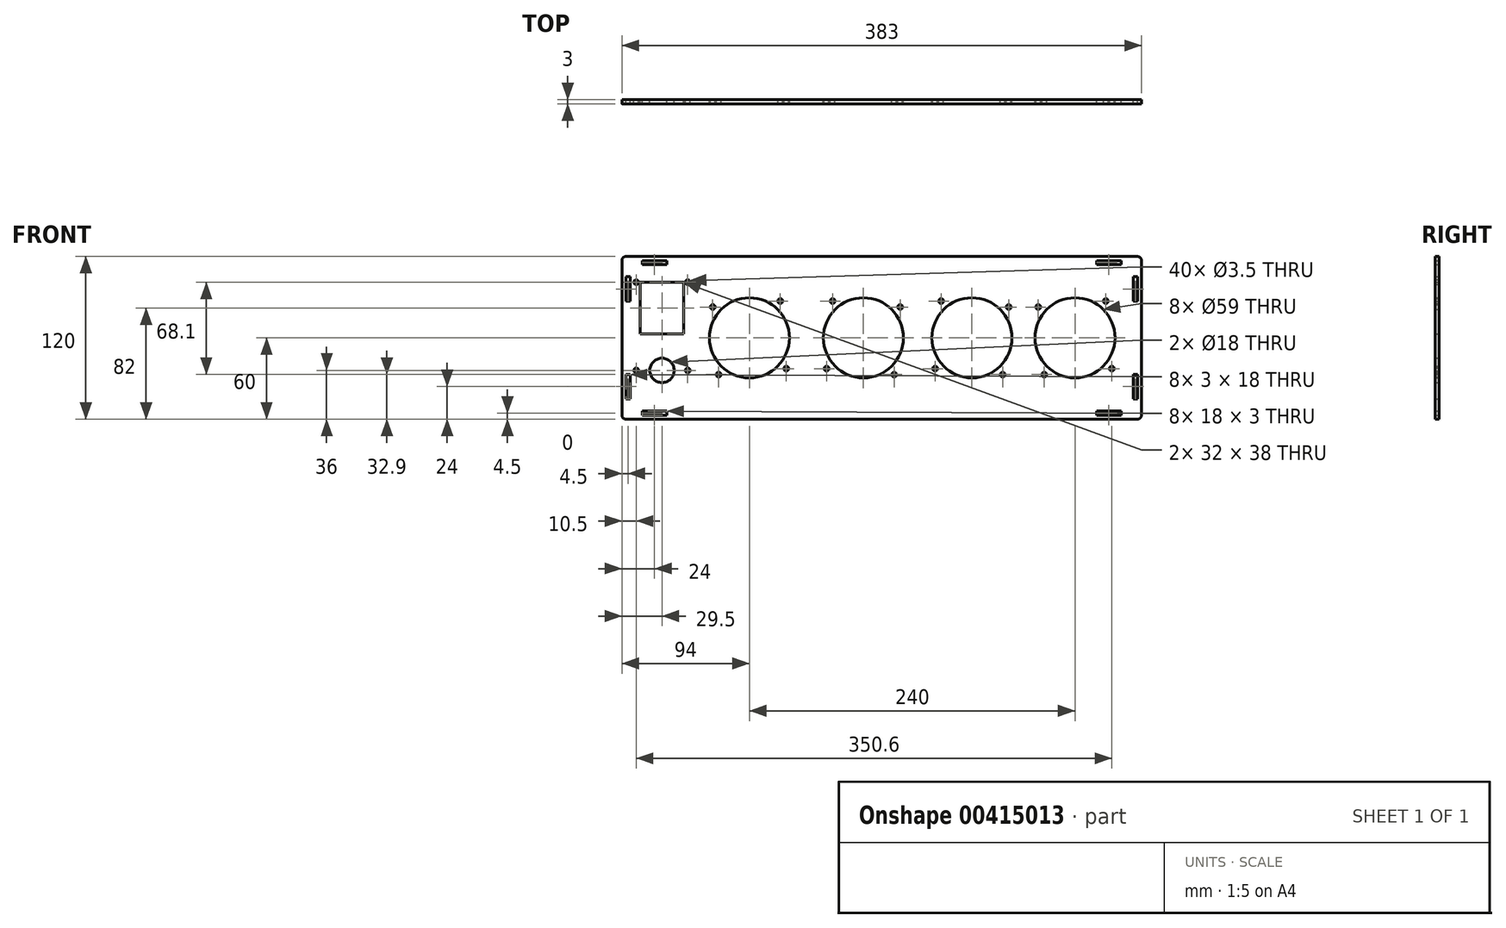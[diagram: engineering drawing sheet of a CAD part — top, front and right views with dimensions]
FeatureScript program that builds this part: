
annotation { "Feature Type Name" : "Feature", "Feature Type Description" : "" }
export const myFeature = defineFeature(function(context is Context, id is Id, definition is map)
    precondition{}
    {
        {
            var Q0;
            Q0=qCreatedBy(makeId("Front.planeOp"),FACE);
            var sketch = newSketch(context, id + "F0", { "sketchPlane" : qUnion([Q0])});
            skLineSegment(sketch, "E0.bottom", {"start": v(-188.5, 60) * mm, "end": v(188.5, 60) * mm});
            skLineSegment(sketch, "E0.top", {"start": v(-188.5, -60) * mm, "end": v(188.5, -60) * mm});
            skLineSegment(sketch, "E0.left", {"start": v(-191.5, 57) * mm, "end": v(-191.5, -57) * mm});
            skLineSegment(sketch, "E0.right", {"start": v(191.5, 57) * mm, "end": v(191.5, -57) * mm});
            skPoint(sketch, "E1.visualSharp", {"position": v(-191.5, 60) * mm});
            skArc(sketch, "E1.filletArc", {"start": v(-188.5, 60) * mm, "mid": v(-190.62, 59.12) * mm, "end": v(-191.5, 57) * mm});
            skPoint(sketch, "E2.visualSharp", {"position": v(191.5, 60) * mm});
            skArc(sketch, "E2.filletArc", {"start": v(191.5, 57) * mm, "mid": v(190.62, 59.12) * mm, "end": v(188.5, 60) * mm});
            skPoint(sketch, "E3.visualSharp", {"position": v(191.5, -60) * mm});
            skArc(sketch, "E3.filletArc", {"start": v(188.5, -60) * mm, "mid": v(190.62, -59.12) * mm, "end": v(191.5, -57) * mm});
            skPoint(sketch, "E4.visualSharp", {"position": v(-191.5, -60) * mm});
            skArc(sketch, "E4.filletArc", {"start": v(-191.5, -57) * mm, "mid": v(-190.62, -59.12) * mm, "end": v(-188.5, -60) * mm});
            skLineSegment(sketch, "E5.bottom", {"start": v(-176.5, 57) * mm, "end": v(-158.5, 57) * mm});
            skLineSegment(sketch, "E5.top", {"start": v(-176.5, 54) * mm, "end": v(-158.5, 54) * mm});
            skLineSegment(sketch, "E5.left", {"start": v(-176.5, 57) * mm, "end": v(-176.5, 54) * mm});
            skLineSegment(sketch, "E5.right", {"start": v(-158.5, 57) * mm, "end": v(-158.5, 54) * mm});
            skLineSegment(sketch, "E6.bottom", {"start": v(158.5, 57) * mm, "end": v(176.5, 57) * mm});
            skLineSegment(sketch, "E6.top", {"start": v(158.5, 54) * mm, "end": v(176.5, 54) * mm});
            skLineSegment(sketch, "E6.left", {"start": v(158.5, 57) * mm, "end": v(158.5, 54) * mm});
            skLineSegment(sketch, "E6.right", {"start": v(176.5, 57) * mm, "end": v(176.5, 54) * mm});
            skLineSegment(sketch, "E7.bottom", {"start": v(188.5, 45) * mm, "end": v(185.5, 45) * mm});
            skLineSegment(sketch, "E7.top", {"start": v(188.5, 27) * mm, "end": v(185.5, 27) * mm});
            skLineSegment(sketch, "E7.left", {"start": v(188.5, 45) * mm, "end": v(188.5, 27) * mm});
            skLineSegment(sketch, "E7.right", {"start": v(185.5, 45) * mm, "end": v(185.5, 27) * mm});
            skLineSegment(sketch, "E8.bottom", {"start": v(188.5, -27) * mm, "end": v(185.5, -27) * mm});
            skLineSegment(sketch, "E8.top", {"start": v(188.5, -45) * mm, "end": v(185.5, -45) * mm});
            skLineSegment(sketch, "E8.left", {"start": v(188.5, -27) * mm, "end": v(188.5, -45) * mm});
            skLineSegment(sketch, "E8.right", {"start": v(185.5, -27) * mm, "end": v(185.5, -45) * mm});
            skLineSegment(sketch, "E9.bottom", {"start": v(176.5, -57) * mm, "end": v(158.5, -57) * mm});
            skLineSegment(sketch, "E9.top", {"start": v(176.5, -54) * mm, "end": v(158.5, -54) * mm});
            skLineSegment(sketch, "E9.left", {"start": v(176.5, -57) * mm, "end": v(176.5, -54) * mm});
            skLineSegment(sketch, "E9.right", {"start": v(158.5, -57) * mm, "end": v(158.5, -54) * mm});
            skLineSegment(sketch, "E10.bottom", {"start": v(-158.5, -57) * mm, "end": v(-176.5, -57) * mm});
            skLineSegment(sketch, "E10.top", {"start": v(-158.5, -54) * mm, "end": v(-176.5, -54) * mm});
            skLineSegment(sketch, "E10.left", {"start": v(-158.5, -57) * mm, "end": v(-158.5, -54) * mm});
            skLineSegment(sketch, "E10.right", {"start": v(-176.5, -57) * mm, "end": v(-176.5, -54) * mm});
            skLineSegment(sketch, "E11.bottom", {"start": v(-185.5, -27) * mm, "end": v(-188.5, -27) * mm});
            skLineSegment(sketch, "E11.top", {"start": v(-185.5, -45) * mm, "end": v(-188.5, -45) * mm});
            skLineSegment(sketch, "E11.left", {"start": v(-185.5, -45) * mm, "end": v(-185.5, -27) * mm});
            skLineSegment(sketch, "E11.right", {"start": v(-188.5, -45) * mm, "end": v(-188.5, -27) * mm});
            skLineSegment(sketch, "E12.bottom", {"start": v(-185.5, 27) * mm, "end": v(-188.5, 27) * mm});
            skLineSegment(sketch, "E12.top", {"start": v(-185.5, 45) * mm, "end": v(-188.5, 45) * mm});
            skLineSegment(sketch, "E12.left", {"start": v(-185.5, 27) * mm, "end": v(-185.5, 45) * mm});
            skLineSegment(sketch, "E12.right", {"start": v(-188.5, 27) * mm, "end": v(-188.5, 45) * mm});
            skCircle(sketch, "E13", {"center": v(142.5, 0) * mm, "radius": 29.5 * mm});
            skCircle(sketch, "E14", {"center": v(165.2, 27.1) * mm, "radius": 1.75 * mm});
            skCircle(sketch, "E15", {"center": v(115.4, 22.7) * mm, "radius": 1.75 * mm});
            skCircle(sketch, "E16", {"center": v(119.8, -27.1) * mm, "radius": 1.75 * mm});
            skCircle(sketch, "E17", {"center": v(169.6, -22.7) * mm, "radius": 1.75 * mm});
            skLineSegment(sketch, "E18", {"start": v(-191.5, 0) * mm, "end": v(191.5, 0) * mm, "construction": true});
            skCircle(sketch, "E19", {"center": v(-162, -24) * mm, "radius": 9 * mm});
            skLineSegment(sketch, "E20", {"start": v(104.5, -5.98) * mm, "end": v(104.5, -18.14) * mm, "construction": true});
            skLineSegment(sketch, "E21.bottom", {"start": v(-178, 41) * mm, "end": v(-146, 41) * mm});
            skLineSegment(sketch, "E21.top", {"start": v(-178, 3) * mm, "end": v(-146, 3) * mm});
            skLineSegment(sketch, "E21.left", {"start": v(-178, 41) * mm, "end": v(-178, 3) * mm});
            skLineSegment(sketch, "E21.right", {"start": v(-146, 41) * mm, "end": v(-146, 3) * mm});
            skLineSegment(sketch, "E22", {"start": v(-162, -24) * mm, "end": v(-162, -20.92) * mm, "construction": true});
            skCircle(sketch, "E23", {"center": v(-181, 41) * mm, "radius": 1.75 * mm});
            skCircle(sketch, "E24", {"center": v(-143, 41) * mm, "radius": 1.75 * mm});
            skCircle(sketch, "E25", {"center": v(-181, -24) * mm, "radius": 1.75 * mm});
            skCircle(sketch, "E26", {"center": v(-143, -24) * mm, "radius": 1.75 * mm});
            skLineSegment(sketch, "E27", {"start": v(24.5, 7.34) * mm, "end": v(24.5, -27.64) * mm, "construction": true});
            skCircle(sketch, "E28.MirrorC", {"center": v(13.6, 22.7) * mm, "radius": 1.75 * mm});
            skCircle(sketch, "E29.MirrorC", {"center": v(-40.6, -22.7) * mm, "radius": 1.75 * mm});
            skCircle(sketch, "E30.MirrorC", {"center": v(9.2, -27.1) * mm, "radius": 1.75 * mm});
            skCircle(sketch, "E31.MirrorC", {"center": v(-36.2, 27.1) * mm, "radius": 1.75 * mm});
            skLineSegment(sketch, "E32.MirrorCS", {"start": v(-55.5, -5.98) * mm, "end": v(-55.5, -18.14) * mm, "construction": true});
            skCircle(sketch, "E33.MirrorC", {"center": v(-13.5, 0) * mm, "radius": 29.5 * mm});
            skCircle(sketch, "E34.MirrorC", {"center": v(-70.4, -22.7) * mm, "radius": 1.75 * mm});
            skCircle(sketch, "E35.MirrorC", {"center": v(-124.6, 22.7) * mm, "radius": 1.75 * mm});
            skCircle(sketch, "E36.MirrorC", {"center": v(-120.2, -27.1) * mm, "radius": 1.75 * mm});
            skCircle(sketch, "E37.MirrorC", {"center": v(-74.8, 27.1) * mm, "radius": 1.75 * mm});
            skLineSegment(sketch, "E38.MirrorCS", {"start": v(-135.5, 7.34) * mm, "end": v(-135.5, -27.64) * mm, "construction": true});
            skCircle(sketch, "E39.MirrorC", {"center": v(-97.5, 0) * mm, "radius": 29.5 * mm});
            skCircle(sketch, "E40.MirrorC", {"center": v(89.2, -27.1) * mm, "radius": 1.75 * mm});
            skCircle(sketch, "E41.MirrorC", {"center": v(39.4, -22.7) * mm, "radius": 1.75 * mm});
            skCircle(sketch, "E42.MirrorC", {"center": v(93.6, 22.7) * mm, "radius": 1.75 * mm});
            skCircle(sketch, "E43.MirrorC", {"center": v(43.8, 27.1) * mm, "radius": 1.75 * mm});
            skCircle(sketch, "E44.MirrorC", {"center": v(66.5, 0) * mm, "radius": 29.5 * mm});
            skSolve(sketch);
        }
        {
            var Q0;
            Q0=makeQuery(id+"F0.imprint","IMPRINT",FACE,{"disambiguationData":[TD([[makeQuery(id+"F0.imprint","IMPRINT",EDGE,{"derivedFrom":sQuery(id+"F0.wireOp",EDGE,"E0.bottom")}),-1.0]])]});
            extrude(context, id + "F1", {"entities" : qUnion([Q0]), "depth" : 3 * mm});
        }
    });
